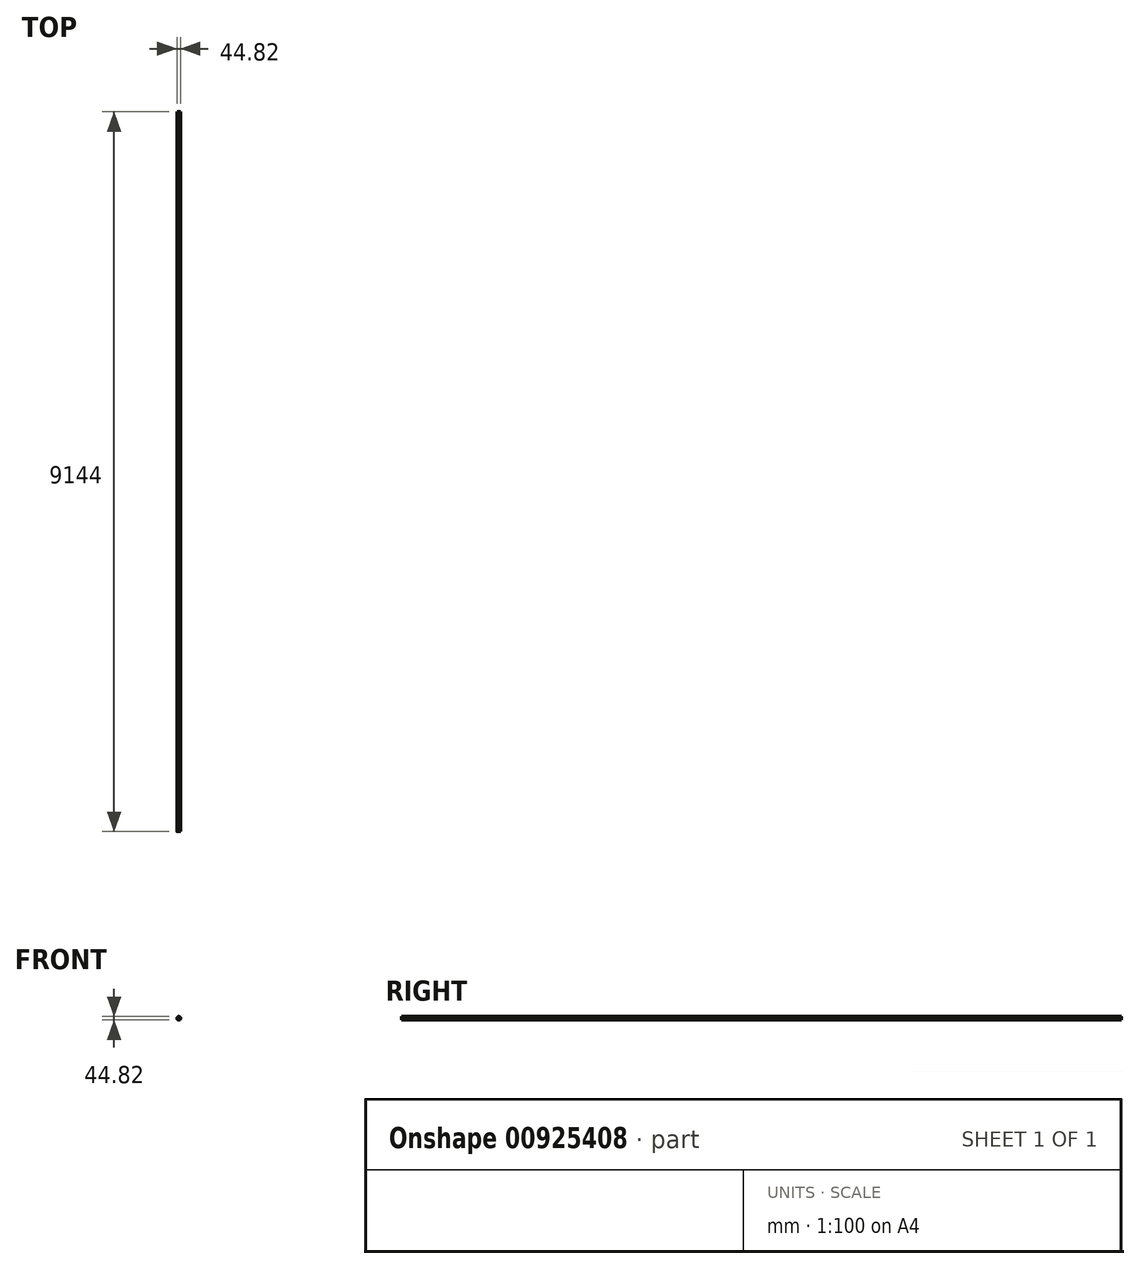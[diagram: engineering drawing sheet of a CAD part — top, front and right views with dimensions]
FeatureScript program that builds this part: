
annotation { "Feature Type Name" : "Feature", "Feature Type Description" : "" }
export const myFeature = defineFeature(function(context is Context, id is Id, definition is map)
    precondition{}
    {
        {
            var Q0;
            Q0=qCreatedBy(makeId("Front.planeOp"),FACE);
            var sketch = newSketch(context, id + "F0", { "sketchPlane" : qUnion([Q0])});
            skCircle(sketch, "E0", {"center": v(0, 0) * mm, "radius": 22.4 * mm});
            skSolve(sketch);
        }
        {
            var Q0;
            Q0 = qSketchRegion(id + "F0", true);
            var Q1;
            Q1=sQuery(id+"F0.wireOp",EDGE,"E0");
            extrude(context, id + "F1", {"entities" : qUnion([Q0]), "bodyType" : ToolBodyType.SURFACE, "surfaceEntities" : qUnion([Q1]), "depth" : 9144 * mm, "offsetDistance" : 25.4 * mm});
        }
    });
